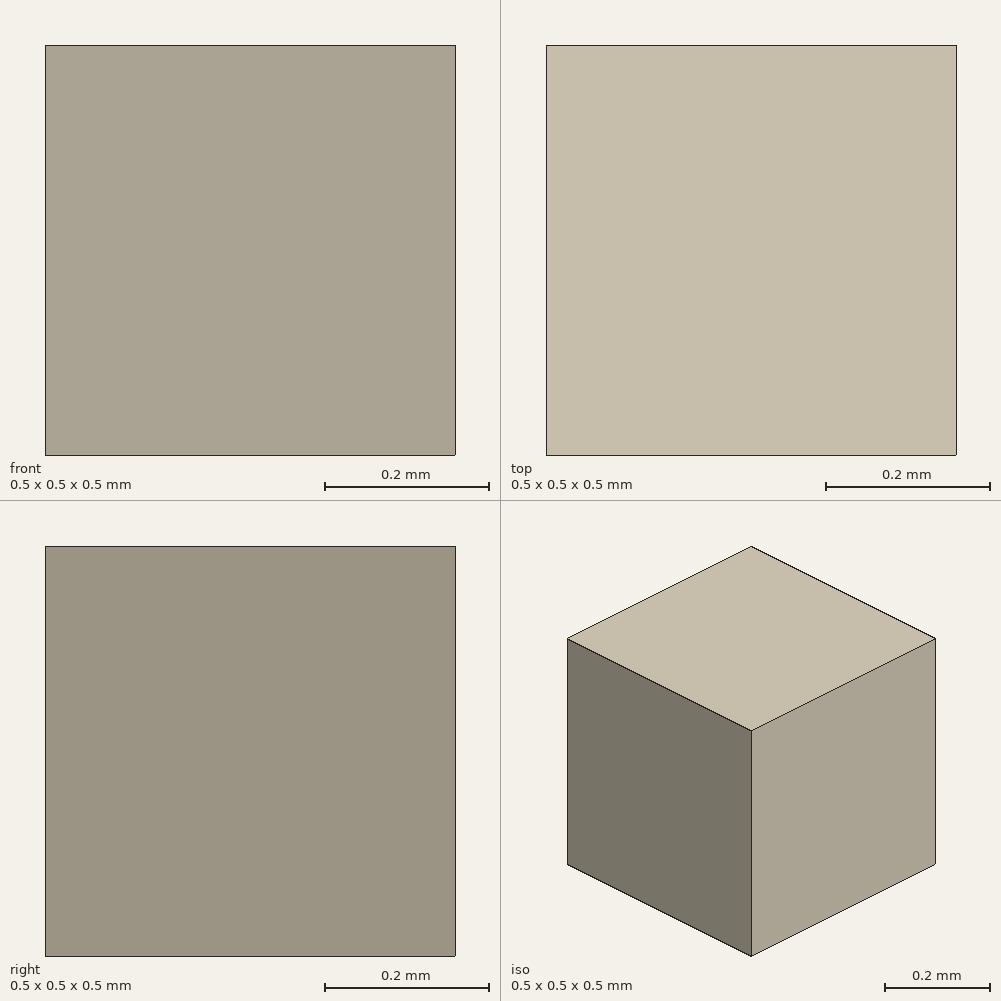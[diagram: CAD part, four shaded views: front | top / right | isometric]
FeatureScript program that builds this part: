
annotation { "Feature Type Name" : "Feature", "Feature Type Description" : "" }
export const myFeature = defineFeature(function(context is Context, id is Id, definition is map)
    precondition{}
    {
        {
            var Q0;
            Q0=qCreatedBy(makeId("Top.planeOp"),FACE);
            var sketch = newSketch(context, id + "F0", { "sketchPlane" : qUnion([Q0])});
            skLineSegment(sketch, "E0.bottom", {"start": v(-6.5, 5.03) * mm, "end": v(-6, 5.03) * mm});
            skLineSegment(sketch, "E0.top", {"start": v(-6.5, 4.53) * mm, "end": v(-6, 4.53) * mm});
            skLineSegment(sketch, "E0.left", {"start": v(-6.5, 5.03) * mm, "end": v(-6.5, 4.53) * mm});
            skLineSegment(sketch, "E0.right", {"start": v(-6, 5.03) * mm, "end": v(-6, 4.53) * mm});
            skSolve(sketch);
        }
        {
            var Q0;
            Q0=makeQuery(id+"F0.imprint","IMPRINT",FACE,{"disambiguationData":[TD([[makeQuery(id+"F0.imprint","IMPRINT",EDGE,{"derivedFrom":sQuery(id+"F0.wireOp",EDGE,"E0.bottom")}),-1.0]])]});
            extrude(context, id + "F1", {"entities" : qUnion([Q0]), "depth" : 0.5 * mm, "offsetDistance" : 25 * mm});
        }
    });
